# Revit family: Toilet-Floor_Mount-KOHLER-REVE-K-17178T
name_source: partatom
category: Plumbing Fixtures
revit_build: Autodesk Revit 2017 (Build: 20160225_1515(x64)
units: mm (PartAtom-declared; Revit-internal decimal feet)

## family parameters
Cut with Voids When Loaded = No
Host = Face
OmniClass Number = 23.31.19.00
OmniClass Title = Toilets
Part Type = Normal
Room Calculation Point = No
Round Connector Dimension = Use Diameter
Shared = No

## types (2) — shared parameters
ADA Compliant = No
Assembly Code = D2010100
CW Connection = Yes
Cold Water Inlet = Cold Water Inlet
Date Modified = 03/23/2021
Default Elevation = 0"
Description = Split Toilet
Finish = Kohler-Vitreous_China-0-White
Flow Rate = 0 GPM
Flush Rate- GPF = 0 GPF
Flush Rate- LPF = 0 LPF
HW Connection = No
Height = 34 5/8"
Hot Water Inlet = Hot Water Inlet
Length = 26 15/16"
Manufacturer = KOHLER Co.
Master Format 2014 = 22 42 13.13
Master Format 2014 Name = Residential Water Closets
Material = Vitreous China
Pressure = 0.00 psi
Product Documentation Link = https://files.kohler.com.cn
Product Name = REVE
Product Page URL = https://www.kohler.com.cn
Rough-In = 7 5/16"
Seat Included = Yes
URL = http://www.kohler.com.cn
Vent Connection = No
Waste Connection = Yes
Waste Water Outlet = Waste Water Outlet
WaterSense Certified = No
Width = 14 9/16"

## per-type parameters (varying)
| type | Ground Drainage | Model | Outlet Connector Diameter 1 | Outlet Connector Diameter 2 | Type | Wall Drainage |
| Wall Drainage,0-White | No | K-17178T-SP2-0 | 2 1/8" | 0" | 1 | Yes |
| Ground Drainage,0-White | Yes | K-17178T-S2-0 | 0" | 2 1/8" | 2 | No |

## geometry (parser evidence)
native form markers: Sweep x4
no freeform markers — native parametric forms only
